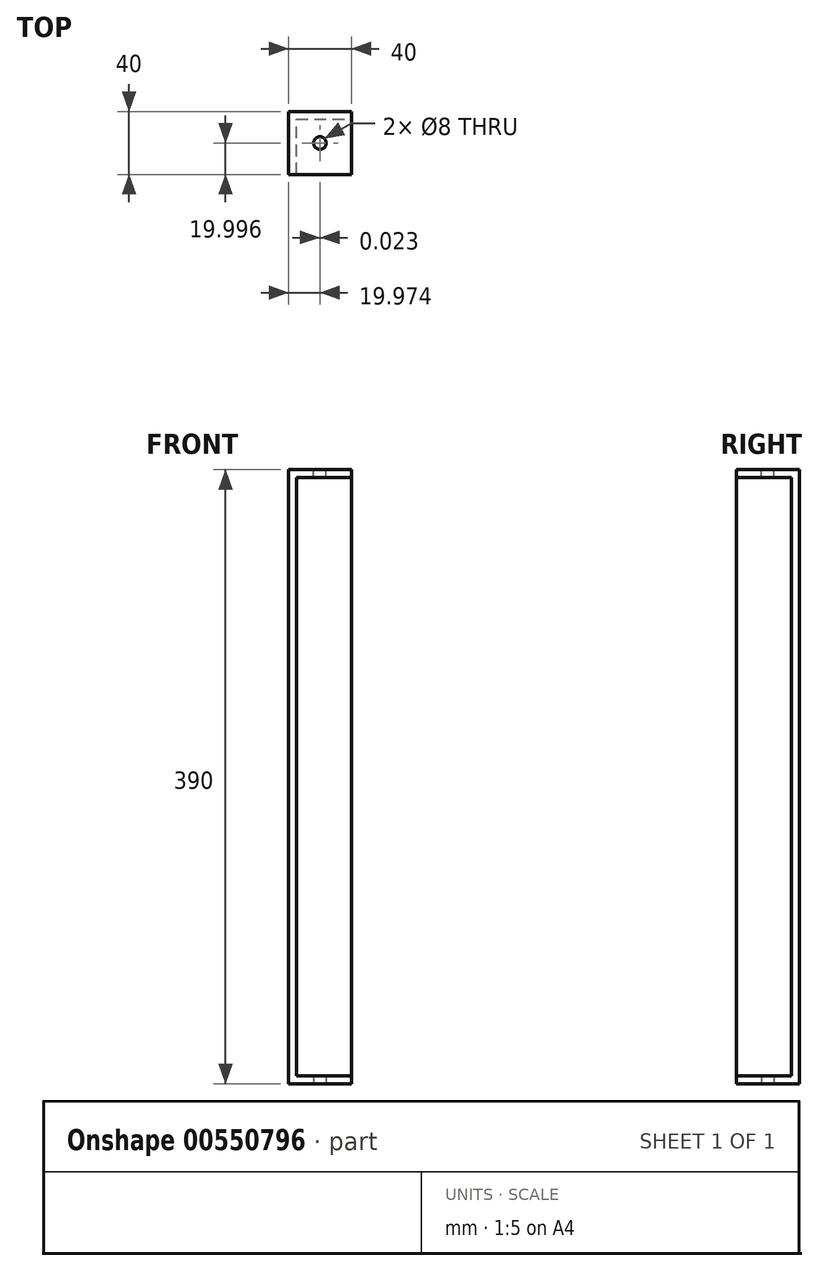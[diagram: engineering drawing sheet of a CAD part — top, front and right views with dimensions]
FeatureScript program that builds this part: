
annotation { "Feature Type Name" : "Feature", "Feature Type Description" : "" }
export const myFeature = defineFeature(function(context is Context, id is Id, definition is map)
    precondition{}
    {
        {
            var Q0;
            Q0=qCreatedBy(makeId("Top.planeOp"),FACE);
            var sketch = newSketch(context, id + "F0", { "sketchPlane" : qUnion([Q0])});
            skLineSegment(sketch, "E0", {"start": v(31.05, 14.66) * mm, "end": v(-8.95, 14.66) * mm});
            skLineSegment(sketch, "E1", {"start": v(-8.95, 14.66) * mm, "end": v(-8.95, -25.34) * mm});
            skLineSegment(sketch, "E2", {"start": v(-8.95, -25.34) * mm, "end": v(-3.95, -25.34) * mm});
            skLineSegment(sketch, "E3", {"start": v(-3.95, -25.34) * mm, "end": v(-3.95, 9.66) * mm});
            skLineSegment(sketch, "E4", {"start": v(-3.95, 9.66) * mm, "end": v(31.05, 9.66) * mm});
            skLineSegment(sketch, "E5", {"start": v(31.05, 9.66) * mm, "end": v(31.05, 14.66) * mm});
            skSolve(sketch);
        }
        {
            var Q0;
            Q0 = qSketchRegion(id + "F0", true);
            extrude(context, id + "F1", {"entities" : qUnion([Q0]), "depth" : 380 * mm, "offsetDistance" : 25 * mm});
        }
        {
            var Q0;
            Q0=makeQuery(id+"F1.opExtrude","CAP_FACE",FACE,{"disambiguationData":[OSD([sQuery(id+"F0.wireOp",EDGE,"E0"),sQuery(id+"F0.wireOp",EDGE,"E1"),sQuery(id+"F0.wireOp",EDGE,"E2"),sQuery(id+"F0.wireOp",EDGE,"E3"),sQuery(id+"F0.wireOp",EDGE,"E4"),sQuery(id+"F0.wireOp",EDGE,"E5")])],"isStart":false});
            var sketch = newSketch(context, id + "F2", { "sketchPlane" : qUnion([Q0])});
            skLineSegment(sketch, "E6", {"start": v(31.05, 14.66) * mm, "end": v(31.05, -25.34) * mm});
            skLineSegment(sketch, "E7", {"start": v(31.05, -25.34) * mm, "end": v(-8.95, -25.34) * mm});
            skLineSegment(sketch, "E8", {"start": v(-8.95, -25.34) * mm, "end": v(-8.95, 14.66) * mm});
            skLineSegment(sketch, "E9", {"start": v(-8.95, 14.66) * mm, "end": v(31.05, 14.66) * mm});
            skSolve(sketch);
        }
        {
            var Q0;
            {var subQ1=sQuery(id+"F2.wireOp",EDGE,"E8");Q0=makeQuery(id+"F2.imprint","IMPRINT",FACE,{"disambiguationData":[TD([[makeQuery(id+"F2.imprint","IMPRINT",EDGE,{"derivedFrom":subQ1}),1.0]])]});}
            var Q1;
            {var subQ4=makeQuery(id+"F1.opExtrude","CAP_EDGE",EDGE,{"disambiguationData":[OSD([sQuery(id+"F0.wireOp",EDGE,"E3")])],"isStart":false});Q1=makeQuery(id+"F2.imprint","IMPRINT",FACE,{"disambiguationData":[TD([[makeQuery(id+"F2.imprint","IMPRINT",EDGE,{"derivedFrom":subQ4}),-1.0]])]});}
            extrude(context, id + "F3", {"entities" : qUnion([Q0, Q1]), "operationType" : NewBodyOperationType.ADD, "depth" : 5 * mm, "offsetDistance" : 25 * mm});
        }
        {
            var Q0;
            Q0=makeQuery(id+"F1.opExtrude","CAP_FACE",FACE,{"disambiguationData":[OSD([sQuery(id+"F0.wireOp",EDGE,"E0"),sQuery(id+"F0.wireOp",EDGE,"E1"),sQuery(id+"F0.wireOp",EDGE,"E2"),sQuery(id+"F0.wireOp",EDGE,"E3"),sQuery(id+"F0.wireOp",EDGE,"E4"),sQuery(id+"F0.wireOp",EDGE,"E5")])],"isStart":true});
            var sketch = newSketch(context, id + "F4", { "sketchPlane" : qUnion([Q0])});
            skLineSegment(sketch, "E10", {"start": v(-8.95, 25.34) * mm, "end": v(31, 25.34) * mm});
            skLineSegment(sketch, "E11", {"start": v(31, 25.34) * mm, "end": v(31.05, -14.66) * mm});
            skLineSegment(sketch, "E12", {"start": v(31.05, -14.66) * mm, "end": v(-8.95, -14.66) * mm});
            skLineSegment(sketch, "E13", {"start": v(-8.95, -14.66) * mm, "end": v(-8.95, 25.34) * mm});
            skSolve(sketch);
        }
        {
            var Q0;
            {var subQ1=sQuery(id+"F4.wireOp",EDGE,"E12");Q0=makeQuery(id+"F4.imprint","IMPRINT",FACE,{"disambiguationData":[TD([[makeQuery(id+"F4.imprint","IMPRINT",EDGE,{"derivedFrom":subQ1}),-1.0]])]});}
            var Q1;
            {var subQ1=makeQuery(id+"F1.opExtrude","CAP_EDGE",EDGE,{"disambiguationData":[OSD([sQuery(id+"F0.wireOp",EDGE,"E3")])],"isStart":true});Q1=makeQuery(id+"F4.imprint","IMPRINT",FACE,{"disambiguationData":[TD([[makeQuery(id+"F4.imprint","IMPRINT",EDGE,{"derivedFrom":subQ1}),1.0]])]});}
            extrude(context, id + "F5", {"entities" : qUnion([Q0, Q1]), "operationType" : NewBodyOperationType.ADD, "depth" : 5 * mm, "offsetDistance" : 25 * mm});
        }
        {
            var Q0;
            Q0=makeQuery(id+"F5.opExtrude","CAP_FACE",FACE,{"disambiguationData":[OSD([sQuery(id+"F4.wireOp",EDGE,"E10"),sQuery(id+"F4.wireOp",EDGE,"E11"),sQuery(id+"F4.wireOp",EDGE,"E12"),sQuery(id+"F4.wireOp",EDGE,"E13")])],"isStart":false});
            var sketch = newSketch(context, id + "F6", { "sketchPlane" : qUnion([Q0])});
            skCircle(sketch, "E14", {"center": v(11.02, 5.34) * mm, "radius": 4 * mm});
            skPoint(sketch, "E14.centerSnap0", {"position": v(31.02, 5.34) * mm});
            skPoint(sketch, "E14.centerSnap1", {"position": v(11.02, 25.34) * mm});
            skSolve(sketch);
        }
        {
            var Q0;
            Q0 = qSketchRegion(id + "F6", true);
            extrude(context, id + "F7", {"entities" : qUnion([Q0]), "operationType" : NewBodyOperationType.REMOVE, "oppositeDirection" : true, "depth" : 25 * mm, "offsetDistance" : 25 * mm});
        }
        {
            var Q0;
            Q0=makeQuery(id+"F3.opExtrude","CAP_FACE",FACE,{"disambiguationData":[OSD([sQuery(id+"F2.wireOp",EDGE,"E6"),sQuery(id+"F2.wireOp",EDGE,"E7"),sQuery(id+"F2.wireOp",EDGE,"E8"),sQuery(id+"F2.wireOp",EDGE,"E9")])],"isStart":false});
            var sketch = newSketch(context, id + "F8", { "sketchPlane" : qUnion([Q0])});
            skCircle(sketch, "E15", {"center": v(11.05, -5.34) * mm, "radius": 4 * mm});
            skPoint(sketch, "E15.centerSnap0", {"position": v(11.05, 14.66) * mm});
            skPoint(sketch, "E15.centerSnap1", {"position": v(31.05, -5.34) * mm});
            skSolve(sketch);
        }
        {
            var Q0;
            Q0=makeQuery(id+"F8.imprint","IMPRINT",FACE,{"disambiguationData":[TD([[makeQuery(id+"F8.imprint","IMPRINT",EDGE,{"derivedFrom":sQuery(id+"F8.wireOp",EDGE,"E15")}),1.0]])]});
            extrude(context, id + "F9", {"entities" : qUnion([Q0]), "operationType" : NewBodyOperationType.REMOVE, "oppositeDirection" : true, "depth" : 25 * mm, "offsetDistance" : 25 * mm});
        }
    });
